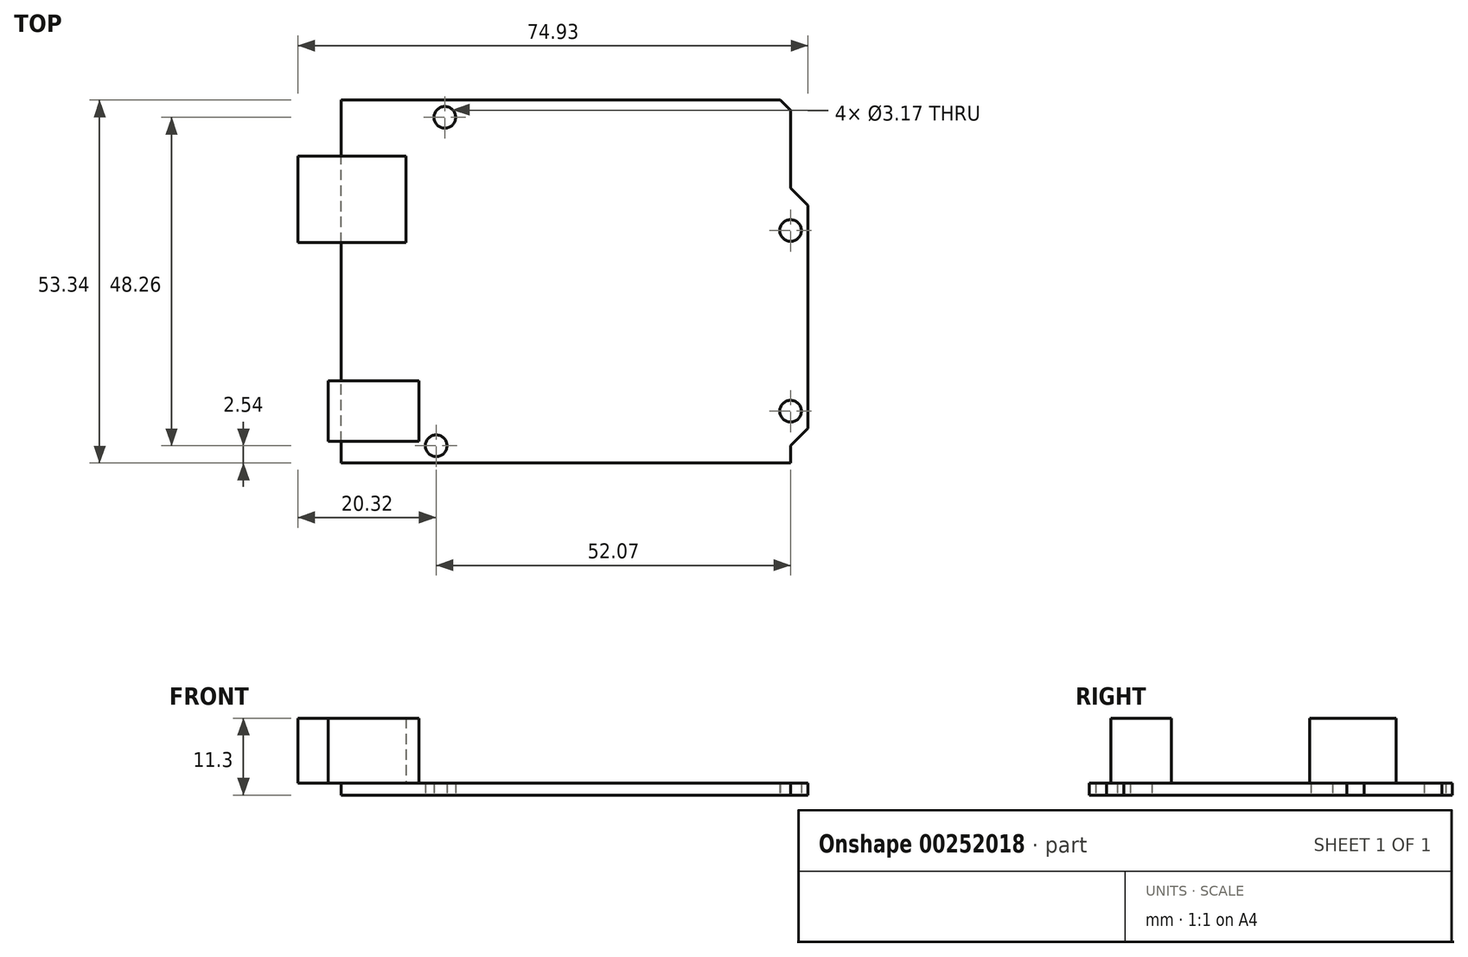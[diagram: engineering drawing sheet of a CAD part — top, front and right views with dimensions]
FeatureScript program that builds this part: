
annotation { "Feature Type Name" : "Feature", "Feature Type Description" : "" }
export const myFeature = defineFeature(function(context is Context, id is Id, definition is map)
    precondition{}
    {
        {
            var Q0;
            Q0=qCreatedBy(makeId("Top.planeOp"),FACE);
            var sketch = newSketch(context, id + "F0", { "sketchPlane" : qUnion([Q0])});
            skLineSegment(sketch, "E0", {"start": v(0, 0) * mm, "end": v(0, 53.34) * mm});
            skLineSegment(sketch, "E1", {"start": v(0, 0) * mm, "end": v(66.04, 0) * mm});
            skLineSegment(sketch, "E2", {"start": v(66.04, 0) * mm, "end": v(66.04, 2.54) * mm});
            skLineSegment(sketch, "E3", {"start": v(66.04, 2.54) * mm, "end": v(68.58, 5.08) * mm});
            skLineSegment(sketch, "E4", {"start": v(68.58, 5.08) * mm, "end": v(68.58, 37.85) * mm});
            skLineSegment(sketch, "E5", {"start": v(66.04, 40.39) * mm, "end": v(68.58, 37.85) * mm});
            skLineSegment(sketch, "E6", {"start": v(66.04, 40.39) * mm, "end": v(66.04, 51.82) * mm});
            skLineSegment(sketch, "E7", {"start": v(0, 53.34) * mm, "end": v(64.52, 53.34) * mm});
            skLineSegment(sketch, "E8", {"start": v(66.04, 51.82) * mm, "end": v(64.52, 53.34) * mm});
            skLineSegment(sketch, "E9", {"start": v(68.58, 7.62) * mm, "end": v(66.04, 7.62) * mm});
            skCircle(sketch, "E10", {"center": v(66.04, 7.62) * mm, "radius": 1.59 * mm});
            skCircle(sketch, "E11", {"center": v(13.97, 2.54) * mm, "radius": 1.59 * mm});
            skLineSegment(sketch, "E12", {"start": v(13.65, 50.8) * mm, "end": v(15.24, 50.8) * mm});
            skCircle(sketch, "E13", {"center": v(15.24, 50.8) * mm, "radius": 1.59 * mm});
            skLineSegment(sketch, "E14", {"start": v(66.04, -1.39) * mm, "end": v(66.04, 34.17) * mm});
            skCircle(sketch, "E15", {"center": v(66.04, 34.17) * mm, "radius": 1.59 * mm});
            skSolve(sketch);
        }
        {
            var Q0;
            Q0 = qSketchRegion(id + "F0", true);
            extrude(context, id + "F1", {"entities" : qUnion([Q0]), "depth" : 1.78 * mm});
        }
        {
            var Q0;
            Q0=makeQuery(id+"F1.opExtrude","CAP_FACE",FACE,{"disambiguationData":[OSD([sQuery(id+"F0.wireOp",EDGE,"E0"),sQuery(id+"F0.wireOp",EDGE,"E1"),sQuery(id+"F0.wireOp",EDGE,"E3"),sQuery(id+"F0.wireOp",EDGE,"E4"),sQuery(id+"F0.wireOp",EDGE,"E5"),sQuery(id+"F0.wireOp",EDGE,"E6"),sQuery(id+"F0.wireOp",EDGE,"E7"),sQuery(id+"F0.wireOp",EDGE,"E8"),sQuery(id+"F0.wireOp",EDGE,"E10"),sQuery(id+"F0.wireOp",EDGE,"E11"),sQuery(id+"F0.wireOp",EDGE,"E13"),sQuery(id+"F0.wireOp",EDGE,"E14"),sQuery(id+"F0.wireOp",EDGE,"E15")])],"isStart":false});
            var sketch = newSketch(context, id + "F2", { "sketchPlane" : qUnion([Q0])});
            skLineSegment(sketch, "E16", {"start": v(9.53, 32.39) * mm, "end": v(0, 32.39) * mm});
            skLineSegment(sketch, "E17", {"start": v(9.53, 32.39) * mm, "end": v(9.53, 45.09) * mm});
            skLineSegment(sketch, "E18", {"start": v(9.53, 45.09) * mm, "end": v(-6.35, 45.09) * mm});
            skLineSegment(sketch, "E19", {"start": v(0, 32.39) * mm, "end": v(-6.35, 32.39) * mm});
            skLineSegment(sketch, "E20", {"start": v(-6.35, 32.39) * mm, "end": v(-6.35, 45.09) * mm});
            skLineSegment(sketch, "E21", {"start": v(11.43, 3.18) * mm, "end": v(0, 3.17) * mm});
            skLineSegment(sketch, "E22", {"start": v(11.43, 3.17) * mm, "end": v(11.43, 12.06) * mm});
            skLineSegment(sketch, "E23", {"start": v(11.43, 12.06) * mm, "end": v(-1.9, 12.06) * mm});
            skLineSegment(sketch, "E24", {"start": v(0, 3.18) * mm, "end": v(-1.9, 3.18) * mm});
            skLineSegment(sketch, "E25", {"start": v(-1.9, 3.18) * mm, "end": v(-1.9, 12.06) * mm});
            skSolve(sketch);
        }
        {
            var Q0;
            Q0 = qSketchRegion(id + "F2", true);
            extrude(context, id + "F3", {"entities" : qUnion([Q0]), "operationType" : NewBodyOperationType.ADD, "depth" : 9.52 * mm});
        }
    });
